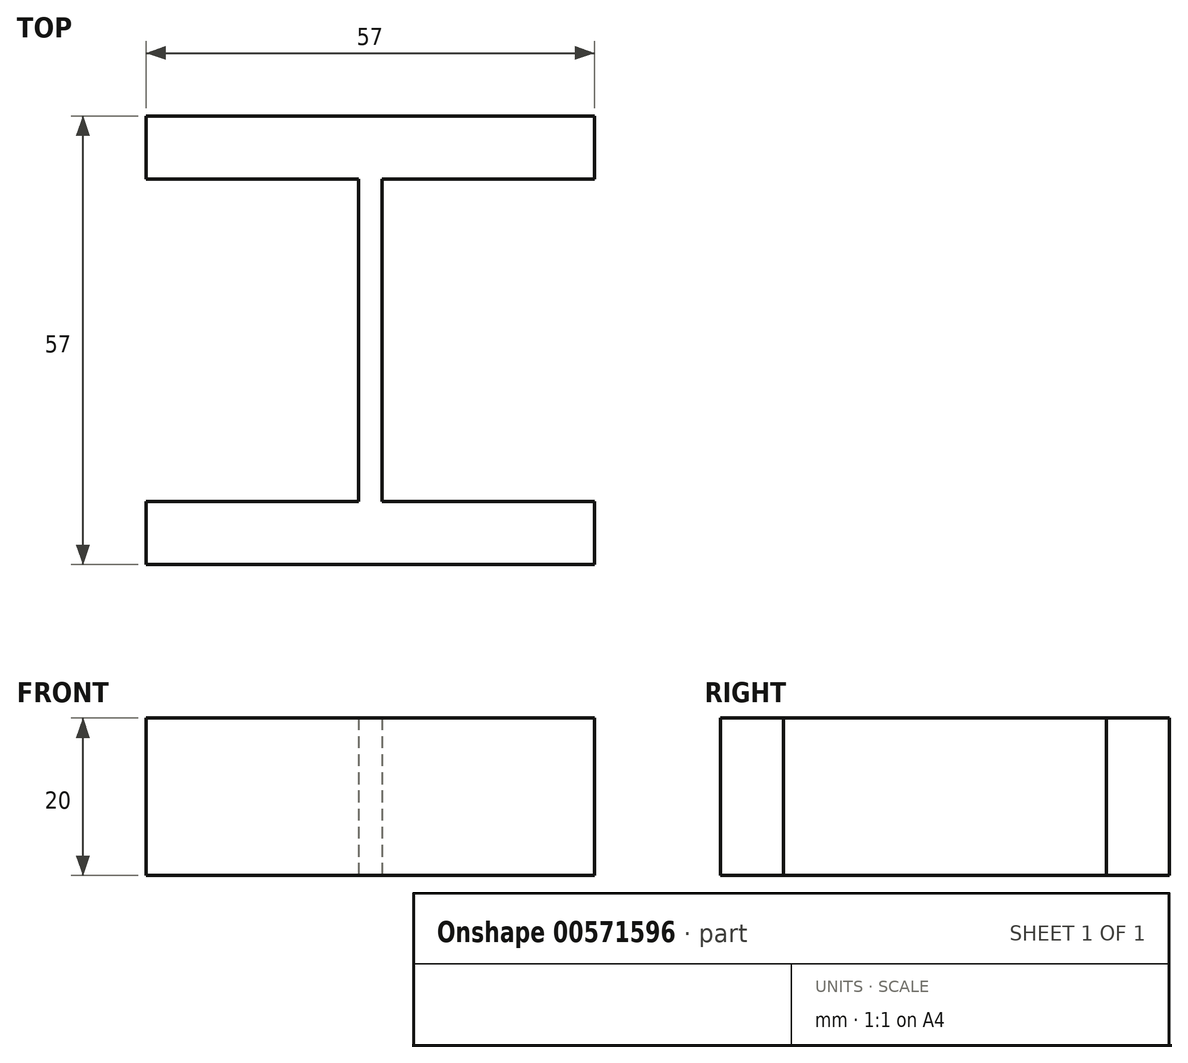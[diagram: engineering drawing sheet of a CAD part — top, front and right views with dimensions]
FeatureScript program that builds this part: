
annotation { "Feature Type Name" : "Feature", "Feature Type Description" : "" }
export const myFeature = defineFeature(function(context is Context, id is Id, definition is map)
    precondition{}
    {
        {
            var Q0;
            Q0=qCreatedBy(makeId("Top.planeOp"),FACE);
            var sketch = newSketch(context, id + "F0", { "sketchPlane" : qUnion([Q0])});
            skLineSegment(sketch, "E0", {"start": v(-64.82, 27.81) * mm, "end": v(-7.82, 27.81) * mm});
            skLineSegment(sketch, "E1", {"start": v(-64.82, 27.81) * mm, "end": v(-64.82, 19.81) * mm});
            skLineSegment(sketch, "E2", {"start": v(-64.82, 19.81) * mm, "end": v(-37.82, 19.81) * mm});
            skLineSegment(sketch, "E3", {"start": v(-7.82, 27.81) * mm, "end": v(-7.82, 19.81) * mm});
            skLineSegment(sketch, "E4", {"start": v(-34.82, 19.81) * mm, "end": v(-7.82, 19.81) * mm});
            skLineSegment(sketch, "E5", {"start": v(-34.82, 19.81) * mm, "end": v(-34.82, -21.19) * mm});
            skLineSegment(sketch, "E6", {"start": v(-37.82, 19.81) * mm, "end": v(-37.82, -21.19) * mm});
            skLineSegment(sketch, "E7", {"start": v(-37.82, -21.19) * mm, "end": v(-64.82, -21.19) * mm});
            skLineSegment(sketch, "E8", {"start": v(-64.82, -21.19) * mm, "end": v(-64.82, -29.19) * mm});
            skLineSegment(sketch, "E9", {"start": v(-64.82, -29.19) * mm, "end": v(-7.82, -29.19) * mm});
            skLineSegment(sketch, "E10", {"start": v(-7.82, -29.19) * mm, "end": v(-7.82, -21.19) * mm});
            skLineSegment(sketch, "E11", {"start": v(-7.82, -21.19) * mm, "end": v(-34.82, -21.19) * mm});
            skSolve(sketch);
        }
        {
            var Q0;
            Q0=makeQuery(id+"F0.imprint","IMPRINT",FACE,{"disambiguationData":[TD([[makeQuery(id+"F0.imprint","IMPRINT",EDGE,{"derivedFrom":sQuery(id+"F0.wireOp",EDGE,"E0")}),-1.0]])]});
            extrude(context, id + "F1", {"entities" : qUnion([Q0]), "depth" : 20 * mm, "offsetDistance" : 25 * mm});
        }
    });
